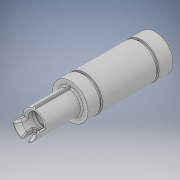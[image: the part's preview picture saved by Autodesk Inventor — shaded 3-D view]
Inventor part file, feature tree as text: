
AUTODESK INVENTOR PART (.ipt)
format: ipt  version: 2019 (Build 230136000, 136)  size: 364,032 bytes
history: native  units: mm
features: chamfer x6, sketch x6, projected_geometry x6, extrude x4, other x2, pattern_linear x1, fillet x1
ambient origin geometry x8: Origin, YZ Plane, XZ Plane, XY Plane, X Axis, Y Axis, Z Axis, Center Point
bodies: Body1 (feature_tree)
feature tree (26):
  other  "Révolution2"
  other  "Révolution3"
  chamfer  "Chanfrein4"  Distance=37.5mm
  pattern_linear  "Réseau rectangulaire1"  Spacing1=14.0mm  [1 undecoded]
  chamfer  "Chanfrein5"  Distance=3.0mm
  extrude  "Extrusion1"  Depth=10.0mm
  chamfer  "Chanfrein6"  Distance=1.0mm
  extrude  "Extrusion5"  Depth=3.0mm
  chamfer  "Chanfrein8"  Distance=0.6mm
  extrude  "Extrusion6"  Depth=1.2mm
  chamfer  "Chanfrein9"  Distance=1.7mm
  extrude  "Extrusion7"  Depth=2.6mm
  fillet  "Congé1"  Radius=24.5mm
  chamfer  "Chanfrein10"  Distance=0.5mm
  sketch  "Esquisse1"
  sketch  "Esquisse2"
  projected_geometry  "Boucle projetée1"
  projected_geometry  "Boucle projetée2"
  sketch  "Esquisse3"
  projected_geometry  "Boucle projetée3"
  sketch  "Esquisse8"
  sketch  "Esquisse9"
  projected_geometry  "Boucle projetée7"
  sketch  "Esquisse10"
  projected_geometry  "Boucle projetée8"
  projected_geometry  "Boucle projetée9"
note: 1 required parameter value undecoded (feature->parameter linkage not recoverable at this tier; creation-order binding heuristic only, values carry confidence <= 0.55)
